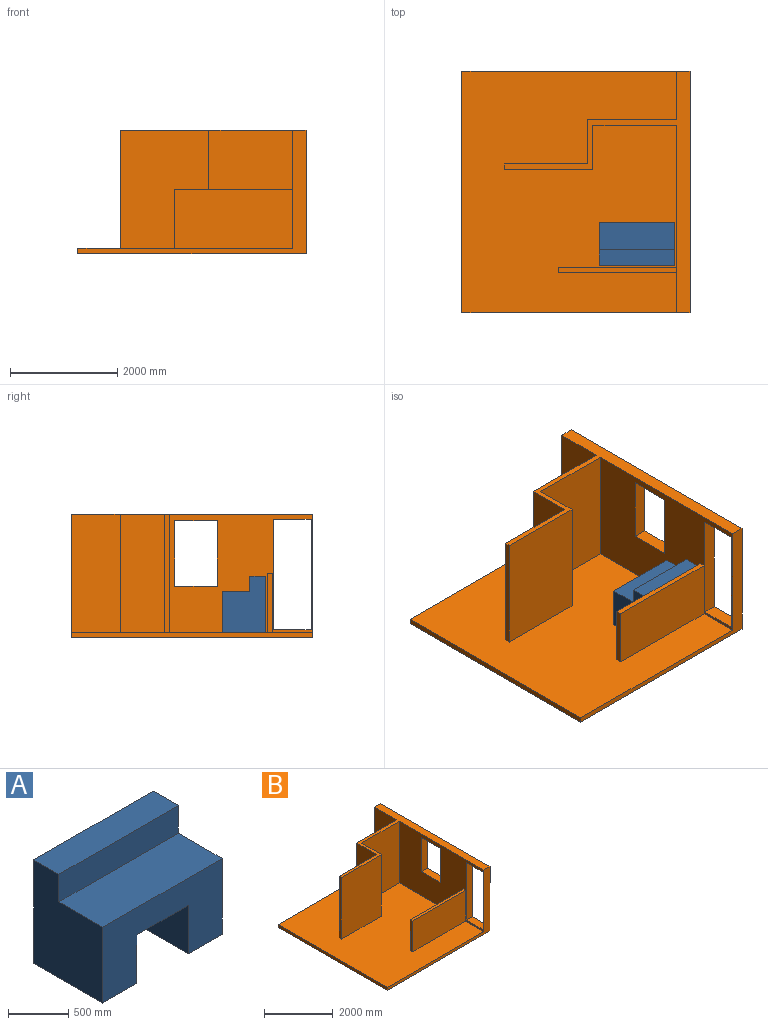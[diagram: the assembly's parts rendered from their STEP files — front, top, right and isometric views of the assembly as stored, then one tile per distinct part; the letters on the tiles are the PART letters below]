
ASSEMBLY  parts=2 mates=1
PART A: 12 faces, bbox 1400x810x1050 mm
  f0: plane 1400x769.15mm, normal (0,-1,0), area 781562.5mm2, adj f1,f3,f5,f6,f7,f8,f9,f10
  f1: plane 1050x810mm, normal (1,0,0), area 705769.4mm2, adj f0,f2,f3,f4,f10,f11
  f2: plane 1400x294.67mm, normal (0,0,1), area 412536.1mm2, adj f1,f4,f5,f11
  f3: plane 810x400mm, normal (0,0,-1), area 324000mm2, adj f0,f1,f4,f8
  f4: plane 1400x1050mm, normal (0,1,0), area 1174751.9mm2, adj f1,f2,f3,f5,f6,f7,f8,f9
  f5: plane 1050x810mm, normal (-1,0,0), area 705769.4mm2, adj f0,f2,f4,f6,f10,f11
  f6: plane 810x400mm, normal (0,0,-1), area 324000mm2, adj f0,f4,f5,f7
  f7: plane 810x492.08mm, normal (1,0,0), area 398584.9mm2, adj f0,f4,f6,f9
  f8: plane 810x492.08mm, normal (-1,0,0), area 398584.9mm2, adj f0,f3,f4,f9
  f9: plane 810x600mm, normal (0,0,-1), area 486000mm2, adj f0,f4,f7,f8
  f10: plane 1400x515.33mm, normal (0,0,1), area 721463.9mm2, adj f0,f1,f5,f11
  f11: plane 1400x280.85mm, normal (0,-1,0), area 393189.5mm2, adj f1,f2,f5,f10
PART B: 28 faces, bbox 4250x4500x2300 mm
  f0: plane 3490x2200mm, normal (-1,0,0), area 5166425.3mm2, adj f2,f5,f9,f10,f16,f18,f19,f20
  f1: plane 4500x2300mm, normal (1,0,0), area 7948425.3mm2, adj f5,f6,f7,f10,f20,f21,f22,f23
  f2: plane 4500x4000mm, normal (0,0,1), area 17377000mm2, adj f0,f3,f4,f5,f6,f8,f9,f11
  f3: plane 2200x820mm, normal (-1,0,0), area 1804000mm2, adj f2,f8,f10,f14
  f4: plane 4500x100mm, normal (-1,0,0), area 450000mm2, adj f2,f5,f6,f7
  f5: plane 4250x2300mm, normal (0,-1,0), area 975000mm2, adj f0,f1,f2,f4,f7,f10
  f6: plane 4250x2300mm, normal (0,1,0), area 975000mm2, adj f1,f2,f4,f7,f10,f15
  f7: plane 4500x4250mm, normal (0,0,-1), area 19125000mm2, adj f1,f4,f5,f6
  f8: plane 2200x1660mm, normal (0,1,0), area 3652000mm2, adj f2,f3,f10,f15
  f9: plane 2200x1560mm, normal (0,-1,0), area 3432000mm2, adj f0,f2,f10,f12
  f10: plane 4500x3460mm, normal (0,0,1), area 1528000mm2, adj f0,f1,f3,f5,f6,f8,f9,f11
  f11: plane 2200x1650mm, normal (0,-1,0), area 3630000mm2, adj f2,f10,f12,f13
  f12: plane 2200x820mm, normal (1,0,0), area 1804000mm2, adj f2,f9,f10,f11
  f13: plane 2200x100mm, normal (-1,0,0), area 220000mm2, adj f2,f10,f11,f14
  f14: plane 2200x1550mm, normal (0,1,0), area 3410000mm2, adj f2,f3,f10,f13
  f15: plane 2200x910mm, normal (-1,0,0), area 2002000mm2, adj f2,f6,f8,f10
  f16: plane 2200x1100mm, normal (0,1,0), area 2420000mm2, adj f0,f2,f17,f19
  f17: plane 1100x100mm, normal (-1,0,0), area 110000mm2, adj f2,f16,f18,f19
  f18: plane 2200x1100mm, normal (0,-1,0), area 2420000mm2, adj f0,f2,f17,f19
  f19: plane 2200x100mm, normal (0,0,1), area 220000mm2, adj f0,f16,f17,f18
  f20: plane 700x250mm, normal (0,0,-1), area 175000mm2, adj f0,f1,f21,f23
  f21: plane 2053.96x250mm, normal (0,-1,0), area 513491mm2, adj f0,f1,f20,f22
  f22: plane 700x250mm, normal (0,0,1), area 175000mm2, adj f0,f1,f21,f23
  f23: plane 2053.96x250mm, normal (0,1,0), area 513491mm2, adj f0,f1,f20,f22
  f24: plane 790x250mm, normal (0,0,-1), area 197500mm2, adj f0,f1,f25,f27
  f25: plane 1220x250mm, normal (0,-1,0), area 305000mm2, adj f0,f1,f24,f26
  f26: plane 790x250mm, normal (0,0,1), area 197500mm2, adj f0,f1,f25,f27
  f27: plane 1220x250mm, normal (0,1,0), area 305000mm2, adj f0,f1,f24,f26
PLACE A rot(axis=(0,0,1),180deg) t=(2973.82,1242.04,-1664.18)mm
PLACE B t=(-986.78,-446.9,-1664.18)mm
MATE planar A.f6 <-> B.f2  axis (0,0,-1) through (2773.82,837.04,-1664.18)mm
